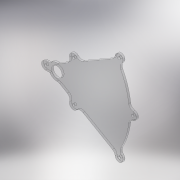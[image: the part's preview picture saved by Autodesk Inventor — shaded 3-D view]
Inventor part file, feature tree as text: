
AUTODESK INVENTOR PART (.ipt)
format: ipt  version: 2018.2 (Build 222227000, 227)  size: 201,216 bytes
history: native  units: mm
features: extrude x2, sketch x1, fillet x1
ambient origin geometry x8: Origin, YZ Plane, XZ Plane, XY Plane, X Axis, Y Axis, Z Axis, Center Point
bodies: Solid1 (feature_tree)
feature tree (4):
  sketch  "Sketch1"  dims[d0=16.0mm d1=101.0mm d3=12.0mm d4=3.0mm d5=0.0mm d6=60.0deg d7=2.0mm d8=5.0mm d9=3.0mm d10=4.0mm d12=5.0mm d13=5.0mm d14=5.0mm d15=5.0mm d16=5.0mm d17=5.0mm d18=25.0mm d19=6.0mm d20=6.0mm d21=3.0mm d22=0.0mm d23=8.0mm]
  extrude  "Extrusion1"  Depth=8.0mm
  extrude  "Extrusion2"  Depth=12.0mm
  fillet  "Fillet1"  Radius=3.0mm
